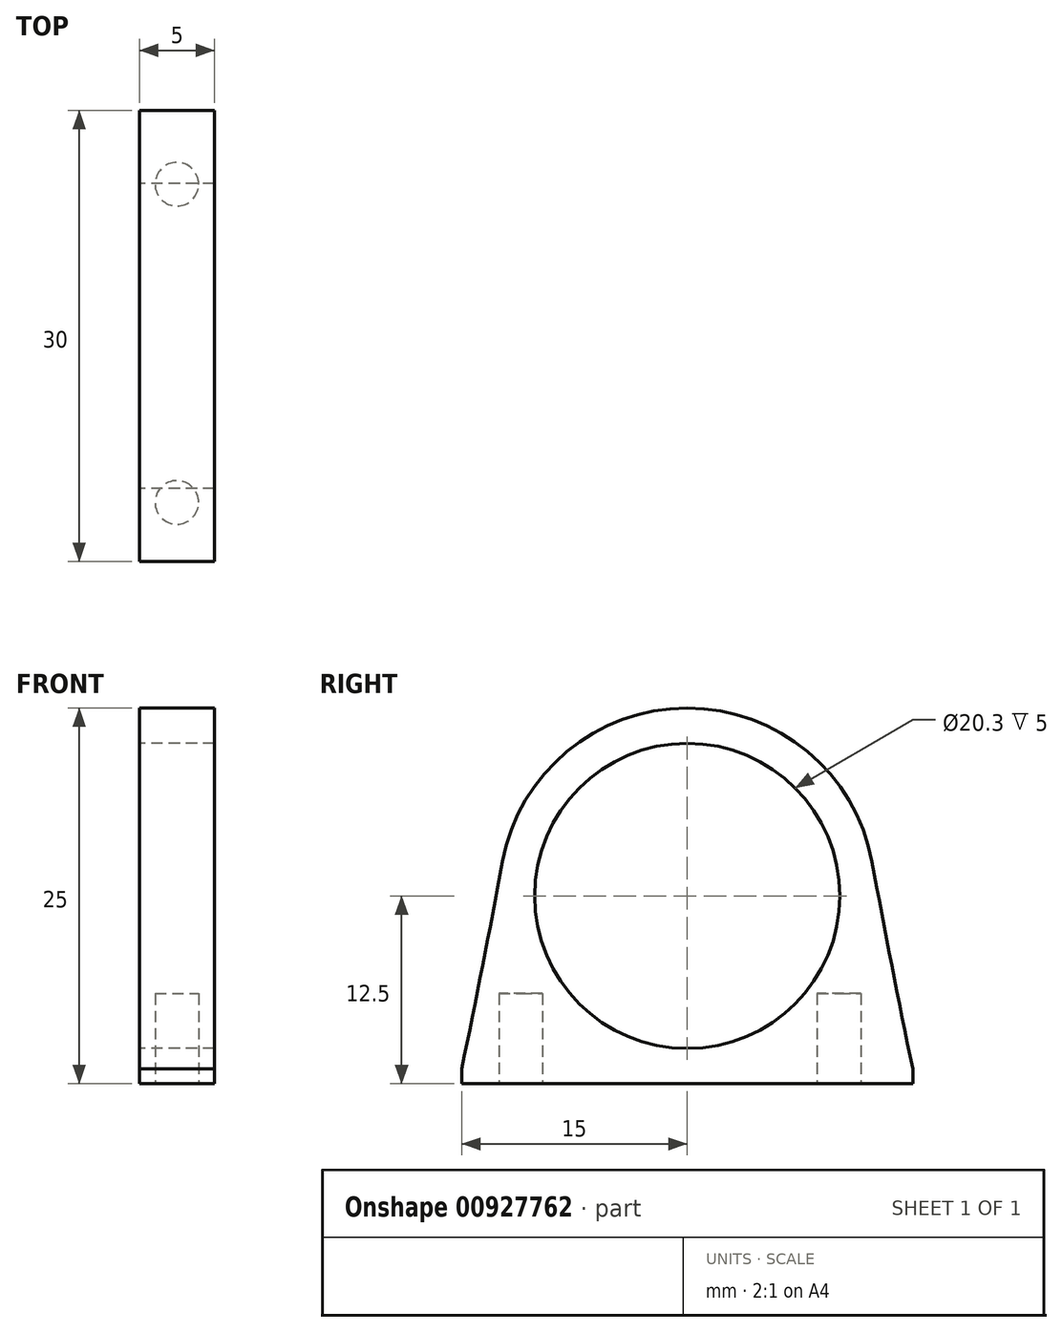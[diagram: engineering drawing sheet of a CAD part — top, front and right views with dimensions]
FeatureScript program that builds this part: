
annotation { "Feature Type Name" : "Feature", "Feature Type Description" : "" }
export const myFeature = defineFeature(function(context is Context, id is Id, definition is map)
    precondition{}
    {
        {
            var Q0;
            Q0=qCreatedBy(makeId("Right.planeOp"),FACE);
            var sketch = newSketch(context, id + "F0", { "sketchPlane" : qUnion([Q0])});
            skCircle(sketch, "E0", {"center": v(0, 0) * mm, "radius": 10.15 * mm});
            skArc(sketch, "E1", {"start": v(12.5, 0) * mm, "mid": v(0, 12.5) * mm, "end": v(-12.5, 0) * mm});
            skLineSegment(sketch, "E2.top", {"start": v(15, -12.5) * mm, "end": v(-15, -12.5) * mm});
            skLineSegment(sketch, "E2.left", {"start": v(15, -11.5) * mm, "end": v(15, -12.5) * mm});
            skLineSegment(sketch, "E2.right", {"start": v(-15, -11.5) * mm, "end": v(-15, -12.5) * mm});
            skLineSegment(sketch, "E3", {"start": v(-12.5, 0) * mm, "end": v(-15, -11.5) * mm});
            skLineSegment(sketch, "E4", {"start": v(12.5, 0) * mm, "end": v(15, -11.5) * mm});
            skLineSegment(sketch, "E5", {"start": v(-15, -11.5) * mm, "end": v(15, -11.5) * mm});
            skSolve(sketch);
        }
        {
            var Q0;
            Q0=makeQuery(id+"F0.imprint","IMPRINT",FACE,{"disambiguationData":[TD([[makeQuery(id+"F0.imprint","IMPRINT",EDGE,{"derivedFrom":sQuery(id+"F0.wireOp",EDGE,"E0")}),-1.0]])]});
            var Q1;
            Q1=makeQuery(id+"F0.imprint","IMPRINT",FACE,{"disambiguationData":[TD([[makeQuery(id+"F0.imprint","IMPRINT",EDGE,{"derivedFrom":sQuery(id+"F0.wireOp",EDGE,"E2.top")}),-1.0]])]});
            extrude(context, id + "F1", {"entities" : qUnion([Q0, Q1]), "depth" : 5 * mm, "offsetDistance" : 25 * mm});
        }
        {
            var Q0;
            Q0=makeQuery(id+"F1.opExtrude","SWEPT_EDGE",EDGE,{"disambiguationData":[OSD([sQuery(id+"F0.wireOp",EDGE,"E1"),sQuery(id+"F0.wireOp",EDGE,"E3")])]});
            var Q1;
            Q1=makeQuery(id+"F1.opExtrude","SWEPT_EDGE",EDGE,{"disambiguationData":[OSD([sQuery(id+"F0.wireOp",EDGE,"E1"),sQuery(id+"F0.wireOp",EDGE,"E4")])]});
            fillet(context, id + "F2", {"entities" : qUnion([Q0, Q1]), "radius" : 608.14 * mm, "tangentPropagation" : true, "allowEdgeOverflow" : false});
        }
        {
            var Q0;
            Q0=makeQuery(id+"F1.opExtrude","SWEPT_FACE",FACE,{"disambiguationData":[OSD([sQuery(id+"F0.wireOp",EDGE,"E2.top")])]});
            var sketch = newSketch(context, id + "F3", { "sketchPlane" : qUnion([Q0])});
            skLineSegment(sketch, "E6", {"start": v(2.5, 15) * mm, "end": v(2.5, -15) * mm, "construction": true});
            skPoint(sketch, "E7", {"position": v(2.5, 0) * mm});
            skPoint(sketch, "E8", {"position": v(2.5, 8.07) * mm});
            skPoint(sketch, "E9", {"position": v(2.5, -7.1) * mm});
            skCircle(sketch, "E10", {"center": v(2.5, 11.07) * mm, "radius": 1.45 * mm});
            skCircle(sketch, "E11", {"center": v(2.5, -10.1) * mm, "radius": 1.45 * mm});
            skSolve(sketch);
        }
        {
            var Q0;
            Q0=makeQuery(id+"F3.imprint","IMPRINT",FACE,{"disambiguationData":[TD([[makeQuery(id+"F3.imprint","IMPRINT",EDGE,{"derivedFrom":sQuery(id+"F3.wireOp",EDGE,"E10")}),1.0]])]});
            var Q1;
            Q1=makeQuery(id+"F3.imprint","IMPRINT",FACE,{"disambiguationData":[TD([[makeQuery(id+"F3.imprint","IMPRINT",EDGE,{"derivedFrom":sQuery(id+"F3.wireOp",EDGE,"E11")}),1.0]])]});
            extrude(context, id + "F4", {"entities" : qUnion([Q0, Q1]), "operationType" : NewBodyOperationType.REMOVE, "oppositeDirection" : true, "depth" : 6 * mm, "offsetDistance" : 25 * mm});
        }
    });
